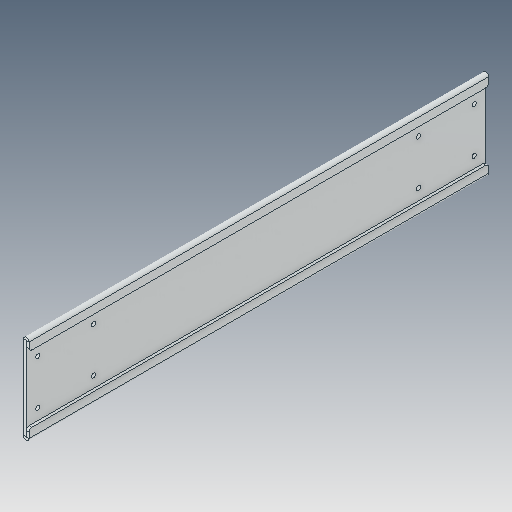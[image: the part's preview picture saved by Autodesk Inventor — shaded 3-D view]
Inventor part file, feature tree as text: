
AUTODESK INVENTOR PART (.ipt)
format: ipt  version: 2023.5 (Build 275446000, 446)  size: 115,200 bytes
history: native  units: in
note: dims shown in document units (in); Inventor stores cm internally (conversion verified against a paired STEP export)
features: fillet x1
ambient origin geometry x8: Origin, YZ Plane, XZ Plane, XY Plane, X Axis, Y Axis, Z Axis, Center Point
bodies: Solid1 (feature_tree)
feature tree (1):
  fillet  "Fillet1"  [1 undecoded]
note: 1 required parameter value undecoded (feature->parameter linkage not recoverable at this tier; creation-order binding heuristic only, values carry confidence <= 0.55)
